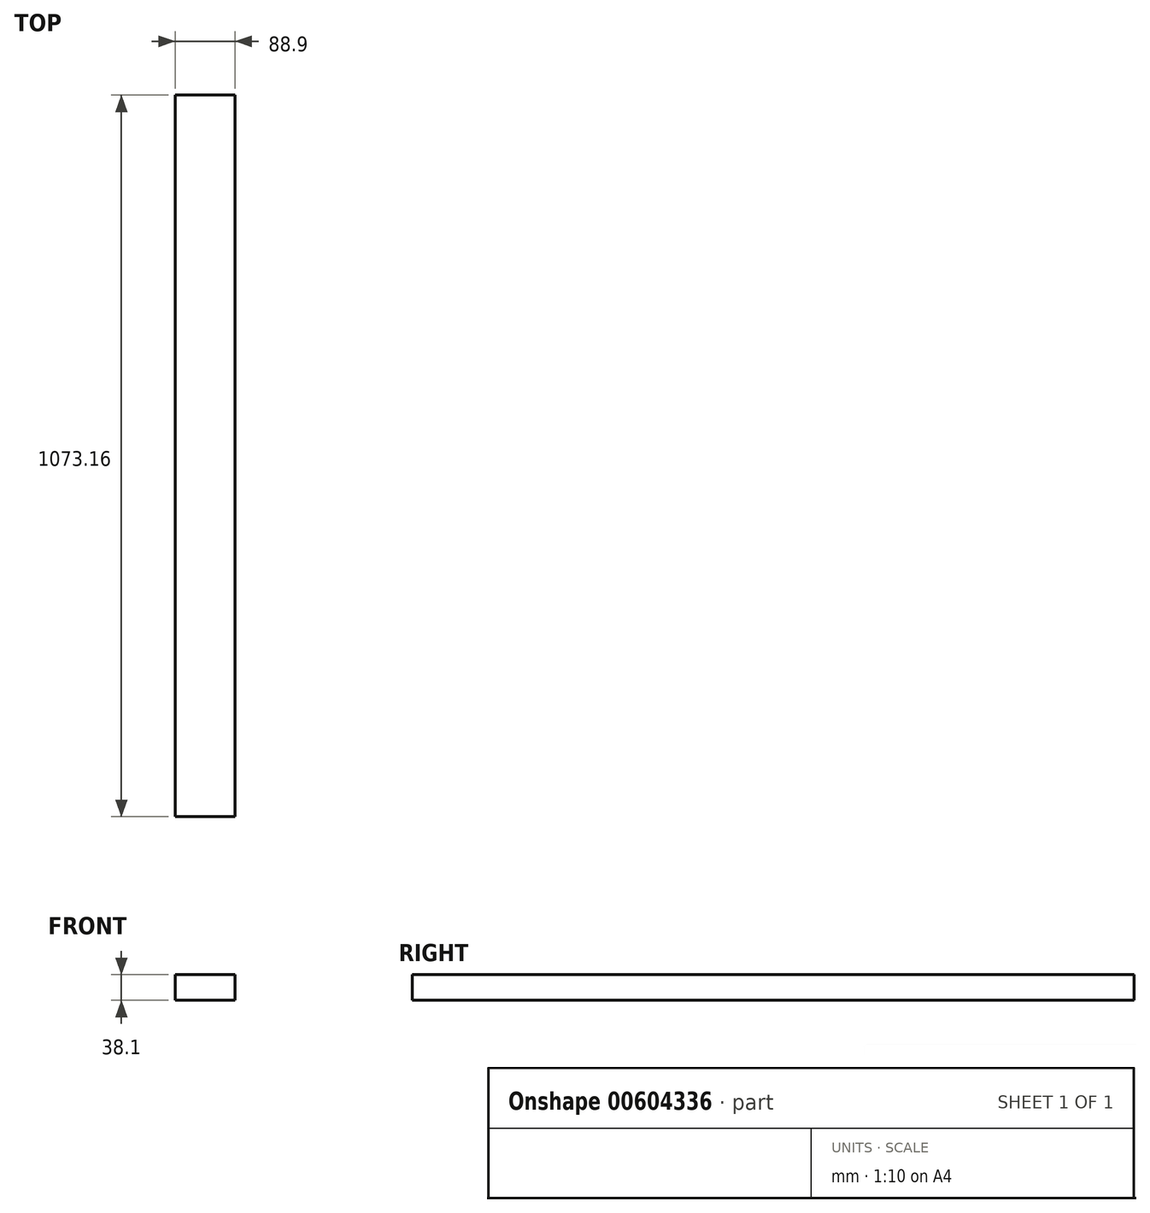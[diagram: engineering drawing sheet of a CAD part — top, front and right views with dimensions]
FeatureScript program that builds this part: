
annotation { "Feature Type Name" : "Feature", "Feature Type Description" : "" }
export const myFeature = defineFeature(function(context is Context, id is Id, definition is map)
    precondition{}
    {
        {
            var Q0;
            Q0=qCreatedBy(makeId("Front.planeOp"),FACE);
            var sketch = newSketch(context, id + "F0", { "sketchPlane" : qUnion([Q0])});
            skLineSegment(sketch, "E0.bottom", {"start": v(44.45, 19.05) * mm, "end": v(-44.45, 19.05) * mm});
            skLineSegment(sketch, "E0.top", {"start": v(44.45, -19.05) * mm, "end": v(-44.45, -19.05) * mm});
            skLineSegment(sketch, "E0.left", {"start": v(44.45, 19.05) * mm, "end": v(44.45, -19.05) * mm});
            skLineSegment(sketch, "E0.right", {"start": v(-44.45, 19.05) * mm, "end": v(-44.45, -19.05) * mm});
            skPoint(sketch, "E0.middle", {"position": v(0, 0) * mm});
            skSolve(sketch);
        }
        {
            var Q0;
            Q0=makeQuery(id+"F0.imprint","IMPRINT",FACE,{"disambiguationData":[TD([[makeQuery(id+"F0.imprint","IMPRINT",EDGE,{"derivedFrom":sQuery(id+"F0.wireOp",EDGE,"E0.bottom")}),1.0]])]});
            extrude(context, id + "F1", {"entities" : qUnion([Q0]), "endBound" : BoundingType.SYMMETRIC, "depth" : 1073.15 * mm, "offsetDistance" : 25.4 * mm});
        }
    });
